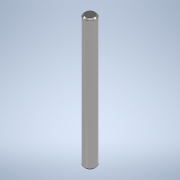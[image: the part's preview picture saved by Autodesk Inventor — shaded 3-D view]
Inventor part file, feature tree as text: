
AUTODESK INVENTOR PART (.ipt)
format: ipt  version: 2021 (Build 250183000, 183)  size: 95,744 bytes
history: native  units: mm
features: extrude x1, chamfer x1, sketch x1
ambient origin geometry x8: Origin, YZ Plane, XZ Plane, XY Plane, X Axis, Y Axis, Z Axis, Center Point
bodies: Solid1 (feature_tree)
feature tree (3):
  extrude  "Extrusion1"  Depth=89.5mm TaperAngle=0.0deg
  chamfer  "Chamfer1"  Distance=1.0mm Angle=45.0deg
  sketch  "Sketch1"  dims[d0=8.0mm d1=89.5mm d2=0.0mm d3=1.0mm d4=2.0mm d5=45.0deg]
